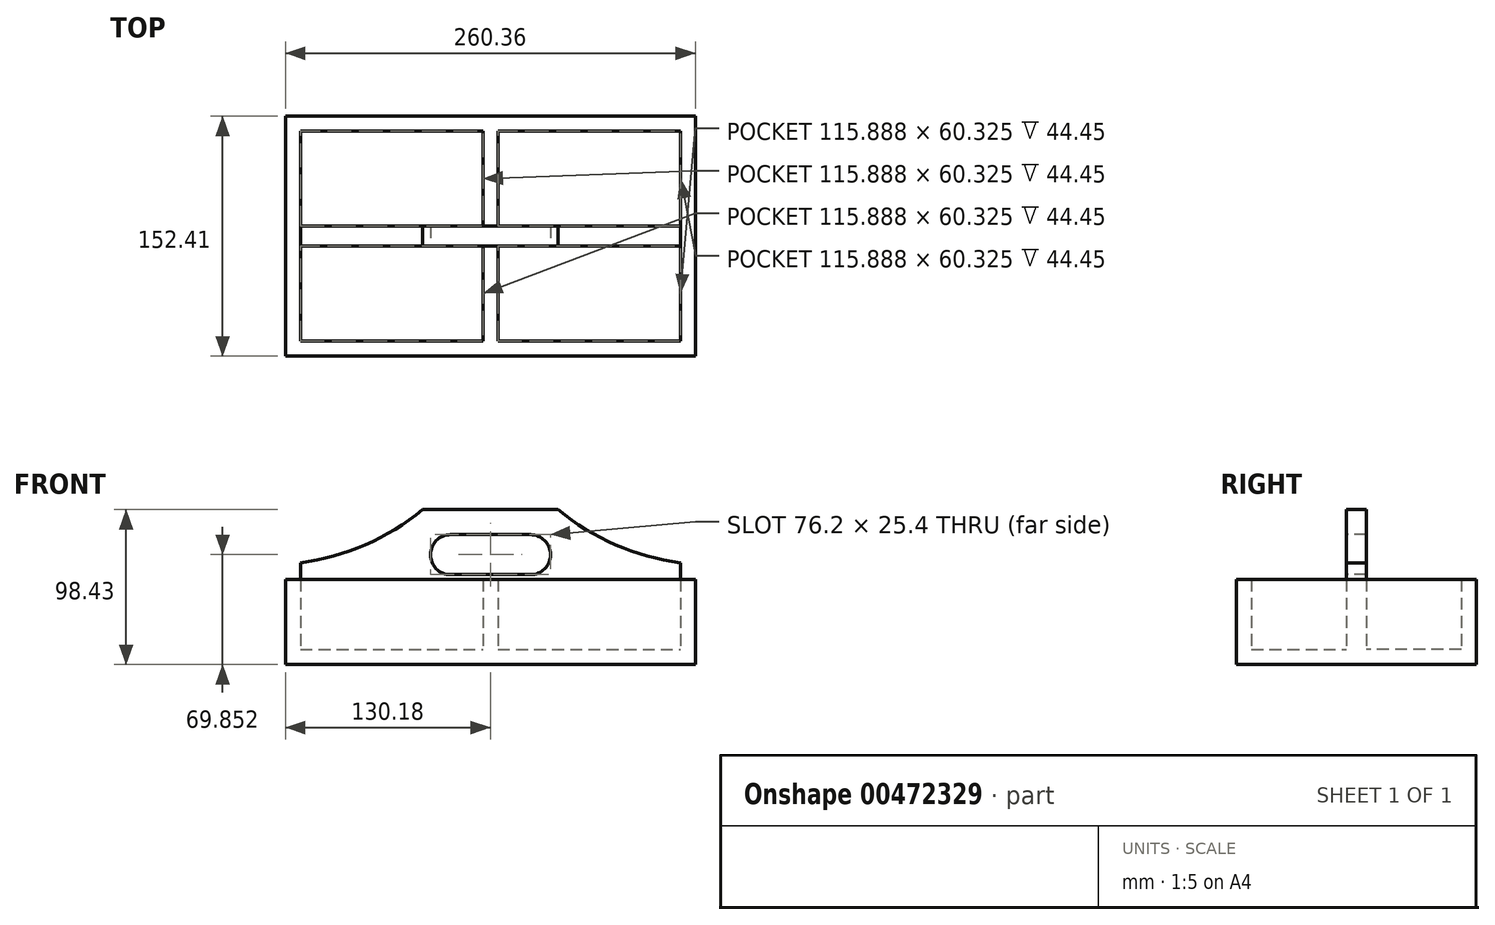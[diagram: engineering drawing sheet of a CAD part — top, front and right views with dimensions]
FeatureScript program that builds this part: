
annotation { "Feature Type Name" : "Feature", "Feature Type Description" : "" }
export const myFeature = defineFeature(function(context is Context, id is Id, definition is map)
    precondition{}
    {
        {
            var Q0;
            Q0=qCreatedBy(makeId("Front.planeOp"),FACE);
            var sketch = newSketch(context, id + "F0", { "sketchPlane" : qUnion([Q0])});
            skLineSegment(sketch, "E0.bottom", {"start": v(-130.18, 26.99) * mm, "end": v(130.18, 26.99) * mm});
            skLineSegment(sketch, "E0.top", {"start": v(-130.18, -26.99) * mm, "end": v(130.18, -26.99) * mm});
            skLineSegment(sketch, "E0.left", {"start": v(-130.18, 26.99) * mm, "end": v(-130.18, -26.99) * mm});
            skLineSegment(sketch, "E0.right", {"start": v(130.18, 26.99) * mm, "end": v(130.18, -26.99) * mm});
            skPoint(sketch, "E0.middle", {"position": v(0, 0) * mm});
            skSolve(sketch);
        }
        {
            var Q0;
            Q0=makeQuery(id+"F0.imprint","IMPRINT",FACE,{"disambiguationData":[TD([[makeQuery(id+"F0.imprint","IMPRINT",EDGE,{"derivedFrom":sQuery(id+"F0.wireOp",EDGE,"E0.bottom")}),-1.0]])]});
            extrude(context, id + "F1", {"entities" : qUnion([Q0]), "depth" : 9.52 * mm});
        }
        {
            var Q0;
            Q0=makeQuery(id+"F1.opExtrude","CAP_FACE",FACE,{"disambiguationData":[OSD([sQuery(id+"F0.wireOp",EDGE,"E0.bottom"),sQuery(id+"F0.wireOp",EDGE,"E0.top"),sQuery(id+"F0.wireOp",EDGE,"E0.left"),sQuery(id+"F0.wireOp",EDGE,"E0.right")])],"isStart":true});
            var sketch = newSketch(context, id + "F2", { "sketchPlane" : qUnion([Q0])});
            skLineSegment(sketch, "E1.bottom", {"start": v(-130.18, 26.99) * mm, "end": v(-120.65, 26.99) * mm});
            skLineSegment(sketch, "E1.top", {"start": v(-130.18, -26.99) * mm, "end": v(-120.65, -26.99) * mm});
            skLineSegment(sketch, "E1.left", {"start": v(-130.18, 26.99) * mm, "end": v(-130.18, -26.99) * mm});
            skLineSegment(sketch, "E1.right", {"start": v(-120.65, 26.99) * mm, "end": v(-120.65, -26.99) * mm});
            skLineSegment(sketch, "E2.bottom", {"start": v(130.18, 26.99) * mm, "end": v(120.65, 26.99) * mm});
            skLineSegment(sketch, "E2.top", {"start": v(130.18, -26.99) * mm, "end": v(120.65, -26.99) * mm});
            skLineSegment(sketch, "E2.left", {"start": v(130.18, 26.99) * mm, "end": v(130.18, -26.99) * mm});
            skLineSegment(sketch, "E2.right", {"start": v(120.65, 26.99) * mm, "end": v(120.65, -26.99) * mm});
            skSolve(sketch);
        }
        {
            var Q0;
            Q0=makeQuery(id+"F2.imprint","IMPRINT",FACE,{"disambiguationData":[TD([[makeQuery(id+"F2.imprint","IMPRINT",EDGE,{"derivedFrom":sQuery(id+"F2.wireOp",EDGE,"E1.bottom")}),1.0]])]});
            var Q1;
            Q1=makeQuery(id+"F2.imprint","IMPRINT",FACE,{"disambiguationData":[TD([[makeQuery(id+"F2.imprint","IMPRINT",EDGE,{"derivedFrom":sQuery(id+"F2.wireOp",EDGE,"E2.bottom")}),1.0]])]});
            extrude(context, id + "F3", {"entities" : qUnion([Q0, Q1]), "operationType" : NewBodyOperationType.ADD, "depth" : 133.35 * mm});
        }
        {
            var Q0;
            Q0=makeQuery(id+"F3.opExtrude","CAP_FACE",FACE,{"disambiguationData":[OSD([sQuery(id+"F2.wireOp",EDGE,"E1.bottom"),sQuery(id+"F2.wireOp",EDGE,"E1.top"),sQuery(id+"F2.wireOp",EDGE,"E1.left"),sQuery(id+"F2.wireOp",EDGE,"E1.right")])],"isStart":false});
            var sketch = newSketch(context, id + "F4", { "sketchPlane" : qUnion([Q0])});
            skLineSegment(sketch, "E3.bottom", {"start": v(-130.18, 26.99) * mm, "end": v(130.18, 26.99) * mm});
            skLineSegment(sketch, "E3.top", {"start": v(-130.18, -26.99) * mm, "end": v(130.18, -26.99) * mm});
            skLineSegment(sketch, "E3.left", {"start": v(-130.18, 26.99) * mm, "end": v(-130.18, -26.99) * mm});
            skLineSegment(sketch, "E3.right", {"start": v(130.18, 26.99) * mm, "end": v(130.18, -26.99) * mm});
            skSolve(sketch);
        }
        {
            var Q0;
            Q0 = qSketchRegion(id + "F4", true);
            extrude(context, id + "F5", {"entities" : qUnion([Q0]), "operationType" : NewBodyOperationType.ADD, "depth" : 9.52 * mm});
        }
        {
            var Q0;
            Q0=makeQuery(id+"F5.opExtrude","CAP_FACE",FACE,{"disambiguationData":[OSD([sQuery(id+"F4.wireOp",EDGE,"E3.bottom"),sQuery(id+"F4.wireOp",EDGE,"E3.top"),sQuery(id+"F4.wireOp",EDGE,"E3.left"),sQuery(id+"F4.wireOp",EDGE,"E3.right")])],"isStart":false});
            var sketch = newSketch(context, id + "F6", { "sketchPlane" : qUnion([Q0])});
            skLineSegment(sketch, "E4.bottom", {"start": v(-130.18, -26.99) * mm, "end": v(130.18, -26.99) * mm});
            skLineSegment(sketch, "E4.top", {"start": v(-130.18, -17.46) * mm, "end": v(130.18, -17.46) * mm});
            skLineSegment(sketch, "E4.left", {"start": v(-130.18, -26.99) * mm, "end": v(-130.18, -17.46) * mm});
            skLineSegment(sketch, "E4.right", {"start": v(130.18, -26.99) * mm, "end": v(130.18, -17.46) * mm});
            skSolve(sketch);
        }
        {
            var Q0;
            Q0=makeQuery(id+"F6.imprint","IMPRINT",FACE,{"disambiguationData":[TD([[makeQuery(id+"F6.imprint","IMPRINT",EDGE,{"derivedFrom":sQuery(id+"F6.wireOp",EDGE,"E4.bottom")}),1.0]])]});
            extrude(context, id + "F7", {"entities" : qUnion([Q0]), "operationType" : NewBodyOperationType.ADD, "oppositeDirection" : true, "depth" : 152.4 * mm});
        }
        {
            var Q0;
            Q0=makeQuery(id+"F7.opExtrude","SWEPT_FACE",FACE,{"disambiguationData":[OSD([sQuery(id+"F6.wireOp",EDGE,"E4.top")])]});
            var sketch = newSketch(context, id + "F8", { "sketchPlane" : qUnion([Q0])});
            skLineSegment(sketch, "E5", {"start": v(-120.65, 66.68) * mm, "end": v(120.65, 66.68) * mm, "construction": true});
            skLineSegment(sketch, "E6.bottom", {"start": v(-120.65, 73.03) * mm, "end": v(120.65, 73.03) * mm});
            skLineSegment(sketch, "E6.top", {"start": v(-120.65, 60.33) * mm, "end": v(120.65, 60.33) * mm});
            skLineSegment(sketch, "E6.left", {"start": v(-120.65, 73.03) * mm, "end": v(-120.65, 60.33) * mm});
            skLineSegment(sketch, "E6.right", {"start": v(120.65, 73.03) * mm, "end": v(120.65, 60.33) * mm});
            skSolve(sketch);
        }
        {
            var Q0;
            Q0 = qSketchRegion(id + "F8", true);
            extrude(context, id + "F9", {"entities" : qUnion([Q0]), "operationType" : NewBodyOperationType.ADD, "depth" : 88.9 * mm});
        }
        {
            var Q0;
            Q0=makeQuery(id+"F9.opExtrude","SWEPT_FACE",FACE,{"disambiguationData":[OSD([sQuery(id+"F8.wireOp",EDGE,"E6.top")])]});
            var sketch = newSketch(context, id + "F10", { "sketchPlane" : qUnion([Q0])});
            skLineSegment(sketch, "E7", {"start": v(0, 71.44) * mm, "end": v(0, 42.86) * mm, "construction": true});
            skPoint(sketch, "E7.endSnap0", {"position": v(0, 71.44) * mm});
            skLineSegment(sketch, "E8", {"start": v(-25.4, 42.86) * mm, "end": v(25.4, 42.86) * mm, "construction": true});
            skArc(sketch, "E9", {"start": v(-25.4, 55.56) * mm, "mid": v(-38.1, 42.86) * mm, "end": v(-25.4, 30.16) * mm});
            skArc(sketch, "E10", {"start": v(25.4, 30.16) * mm, "mid": v(38.1, 42.86) * mm, "end": v(25.4, 55.56) * mm});
            skLineSegment(sketch, "E11", {"start": v(-25.4, 55.56) * mm, "end": v(25.4, 55.56) * mm});
            skLineSegment(sketch, "E12", {"start": v(-25.4, 30.16) * mm, "end": v(25.4, 30.16) * mm});
            skLineSegment(sketch, "E13", {"start": v(-25.4, 55.56) * mm, "end": v(-25.4, 30.16) * mm, "construction": true});
            skLineSegment(sketch, "E14", {"start": v(25.4, 55.56) * mm, "end": v(25.4, 30.16) * mm, "construction": true});
            skSolve(sketch);
        }
        {
            var Q0;
            Q0 = qSketchRegion(id + "F10", true);
            extrude(context, id + "F11", {"entities" : qUnion([Q0]), "operationType" : NewBodyOperationType.REMOVE, "oppositeDirection" : true, "depth" : 12.7 * mm});
        }
        {
            var Q0;
            Q0=qCreatedBy(makeId("Front.planeOp"),FACE);
            var sketch = newSketch(context, id + "F12", { "sketchPlane" : qUnion([Q0])});
            skLineSegment(sketch, "E15", {"start": v(130.18, -26.99) * mm, "end": v(130.18, 188.91) * mm, "construction": true});
            skLineSegment(sketch, "E16", {"start": v(-130.18, -26.99) * mm, "end": v(-130.18, 188.91) * mm, "construction": true});
            skLineSegment(sketch, "E17", {"start": v(-130.18, 188.91) * mm, "end": v(-140.18, 188.91) * mm, "construction": true});
            skLineSegment(sketch, "E18", {"start": v(130.18, 188.91) * mm, "end": v(140.18, 188.91) * mm, "construction": true});
            skCircle(sketch, "E19", {"center": v(-140.18, 188.91) * mm, "radius": 152.4 * mm});
            skCircle(sketch, "E20", {"center": v(140.18, 188.91) * mm, "radius": 152.4 * mm});
            skSolve(sketch);
        }
        {
            var Q0;
            {var subQ0=sQuery(id+"F12.wireOp",EDGE,"E20");var subQ1=sQuery(id+"F12.wireOp",EDGE,"E19");var subQ2=makeQuery(id+"F12.imprint","INTERSECT",VERTEX,{"disambiguationData":[OD(0.0)],"derivedFrom":[subQ1,subQ0]});Q0=makeQuery(id+"F12.imprint","IMPRINT",FACE,{"disambiguationData":[TD([[makeQuery(id+"F12.imprint","IMPRINT",EDGE,{"disambiguationData":[TD([[subQ2,1.0]])],"derivedFrom":subQ1}),1.0]])]});}
            var Q1;
            {var subQ0=sQuery(id+"F12.wireOp",EDGE,"E20");var subQ1=sQuery(id+"F12.wireOp",EDGE,"E19");var subQ2=makeQuery(id+"F12.imprint","INTERSECT",VERTEX,{"disambiguationData":[OD(0.0)],"derivedFrom":[subQ1,subQ0]});Q1=makeQuery(id+"F12.imprint","IMPRINT",FACE,{"disambiguationData":[TD([[makeQuery(id+"F12.imprint","IMPRINT",EDGE,{"disambiguationData":[TD([[subQ2,-1.0]])],"derivedFrom":subQ1}),-1.0]])]});}
            extrude(context, id + "F13", {"entities" : qUnion([Q0, Q1]), "operationType" : NewBodyOperationType.REMOVE, "oppositeDirection" : true, "depth" : 102.1 * mm});
        }
        {
            var Q0;
            Q0=makeQuery(id+"F9.boolean.opBoolean","SPLIT",FACE,{"disambiguationData":[TD([makeQuery(id+"F9.opExtrude","SWEPT_FACE",FACE,{"disambiguationData":[OSD([sQuery(id+"F8.wireOp",EDGE,"E6.bottom")])]})])],"derivedFrom":makeQuery(id+"F7.opExtrude","SWEPT_FACE",FACE,{"disambiguationData":[OSD([sQuery(id+"F6.wireOp",EDGE,"E4.top")])]})});
            var sketch = newSketch(context, id + "F14", { "sketchPlane" : qUnion([Q0])});
            skLineSegment(sketch, "E21", {"start": v(-120.65, 133.35) * mm, "end": v(-4.76, 133.35) * mm, "construction": true});
            skLineSegment(sketch, "E22.bottom", {"start": v(-4.76, 133.35) * mm, "end": v(4.76, 133.35) * mm});
            skLineSegment(sketch, "E22.top", {"start": v(-4.76, 73.03) * mm, "end": v(4.76, 73.03) * mm});
            skLineSegment(sketch, "E22.left", {"start": v(-4.76, 133.35) * mm, "end": v(-4.76, 73.03) * mm});
            skLineSegment(sketch, "E22.right", {"start": v(4.76, 133.35) * mm, "end": v(4.76, 73.03) * mm});
            skSolve(sketch);
        }
        {
            var Q0;
            Q0=makeQuery(id+"F14.imprint","IMPRINT",FACE,{"disambiguationData":[TD([[makeQuery(id+"F14.imprint","IMPRINT",EDGE,{"derivedFrom":sQuery(id+"F14.wireOp",EDGE,"E22.bottom")}),1.0]])]});
            extrude(context, id + "F15", {"entities" : qUnion([Q0]), "operationType" : NewBodyOperationType.ADD, "depth" : 44.45 * mm});
        }
        {
            var Q0;
            Q0=makeQuery(id+"F9.boolean.opBoolean","SPLIT",FACE,{"disambiguationData":[TD([makeQuery(id+"F9.opExtrude","SWEPT_FACE",FACE,{"disambiguationData":[OSD([sQuery(id+"F8.wireOp",EDGE,"E6.top")])]})])],"derivedFrom":makeQuery(id+"F7.opExtrude","SWEPT_FACE",FACE,{"disambiguationData":[OSD([sQuery(id+"F6.wireOp",EDGE,"E4.top")])]})});
            var sketch = newSketch(context, id + "F16", { "sketchPlane" : qUnion([Q0])});
            skLineSegment(sketch, "E23", {"start": v(-120.65, 0) * mm, "end": v(-4.76, 0) * mm, "construction": true});
            skLineSegment(sketch, "E24.bottom", {"start": v(-4.76, 0) * mm, "end": v(4.76, 0) * mm});
            skLineSegment(sketch, "E24.top", {"start": v(-4.76, 60.33) * mm, "end": v(4.76, 60.33) * mm});
            skLineSegment(sketch, "E24.left", {"start": v(-4.76, 0) * mm, "end": v(-4.76, 60.33) * mm});
            skLineSegment(sketch, "E24.right", {"start": v(4.76, 0) * mm, "end": v(4.76, 60.33) * mm});
            skSolve(sketch);
        }
        {
            var Q0;
            Q0=makeQuery(id+"F16.imprint","IMPRINT",FACE,{"disambiguationData":[TD([[makeQuery(id+"F16.imprint","IMPRINT",EDGE,{"derivedFrom":sQuery(id+"F16.wireOp",EDGE,"E24.bottom")}),1.0]])]});
            extrude(context, id + "F17", {"entities" : qUnion([Q0]), "operationType" : NewBodyOperationType.ADD, "depth" : 44.45 * mm});
        }
    });
